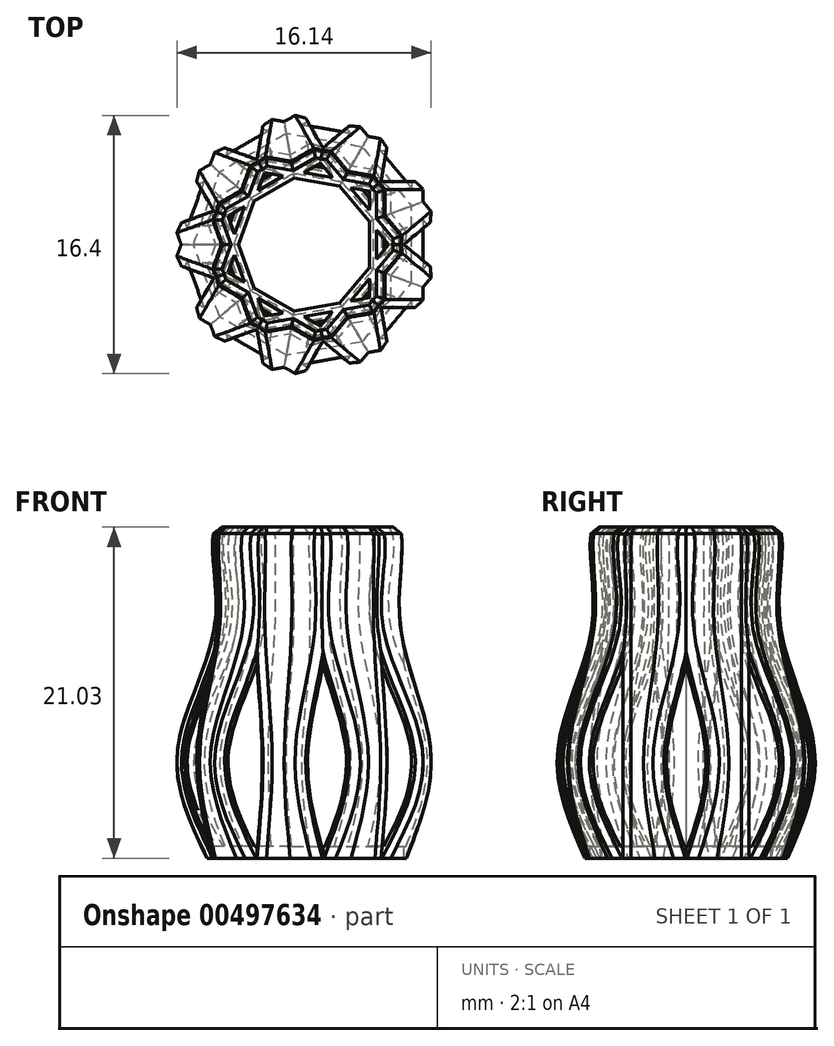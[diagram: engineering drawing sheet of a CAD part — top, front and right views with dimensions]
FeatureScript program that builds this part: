
annotation { "Feature Type Name" : "Feature", "Feature Type Description" : "" }
export const myFeature = defineFeature(function(context is Context, id is Id, definition is map)
    precondition{}
    {
        {
            var Q0;
            Q0=qCreatedBy(makeId("Front.planeOp"),FACE);
            var sketch = newSketch(context, id + "F0", { "sketchPlane" : qUnion([Q0])});
            skLineSegment(sketch, "E0", {"start": v(0, 0) * mm, "end": v(5.4, 0) * mm});
            skLineSegment(sketch, "E1", {"start": v(0, 2.1) * mm, "end": v(0, 0) * mm});
            skLineSegment(sketch, "E2.0", {"start": v(0, 0.75) * mm, "end": v(4.94, 0.75) * mm});
            skFitSpline(sketch, "E3", {"points": [v(5.4, 0) * mm, v(7.42, 6.77) * mm, v(4.86, 15) * mm, v(4.86, 21.03) * mm, v(2.2, 23.07) * mm], "startDerivative": vector(12.6, 24.53) * mm, "endDerivative": vector(-18.36, 8.19) * mm});
            skFitSpline(sketch, "E4.0", {"points": [v(4.73, 0.34) * mm, v(5, 0.85) * mm, v(5.52, 1.86) * mm, v(6.17, 3.35) * mm, v(6.54, 4.57) * mm, v(6.69, 5.53) * mm, v(6.72, 6.25) * mm, v(6.65, 6.97) * mm, v(6.5, 7.74) * mm, v(6.25, 8.54) * mm, v(5.85, 9.64) * mm, v(5.37, 10.8) * mm, v(4.9, 11.99) * mm, v(4.57, 12.9) * mm, v(4.3, 13.83) * mm, v(4.14, 14.63) * mm, v(4.07, 15.28) * mm, v(4.04, 15.91) * mm, v(4.05, 17) * mm, v(4.17, 18.14) * mm, v(4.26, 19.14) * mm, v(4.3, 19.8) * mm, v(4.27, 20.26) * mm, v(4.22, 20.56) * mm, v(4.17, 20.75) * mm, v(4.1, 20.9) * mm, v(3.98, 21.1) * mm, v(3.77, 21.34) * mm, v(3.42, 21.62) * mm, v(2.83, 21.97) * mm, v(2.28, 22.22) * mm, v(1.9, 22.39) * mm]});
            skLineSegment(sketch, "E5", {"start": v(1.9, 22.39) * mm, "end": v(3.6, 22.39) * mm});
            skPoint(sketch, "E6.orphan", {"position": v(4.86, 0.75) * mm});
            skLineSegment(sketch, "E7", {"start": v(4.86, 21.03) * mm, "end": v(2.46, 21.03) * mm});
            skSolve(sketch);
        }
        {
            var Q0;
            {var subQ2=sQuery(id+"F0.wireOp",EDGE,"E0");Q0=makeQuery(id+"F0.imprint","IMPRINT",FACE,{"disambiguationData":[TD([[makeQuery(id+"F0.imprint","IMPRINT",EDGE,{"derivedFrom":subQ2}),1.0]])]});}
            extrude(context, id + "F1", {"entities" : qUnion([Q0]), "depth" : 4 * mm, "hasSecondDirection" : true, "secondDirectionOppositeDirection" : true, "secondDirectionDepth" : 4 * mm});
        }
        {
            var Q0;
            Q0=makeQuery(id+"F1.opExtrude","CAP_EDGE",EDGE,{"disambiguationData":[OSD([sQuery(id+"F0.wireOp",EDGE,"E3")])],"isStart":false});
            var Q1;
            Q1=makeQuery(id+"F1.opExtrude","CAP_EDGE",EDGE,{"disambiguationData":[OSD([sQuery(id+"F0.wireOp",EDGE,"E3")])],"isStart":true});
            chamfer(context, id + "F2", {"entities" : qUnion([Q0, Q1]), "width" : 0.5 * mm});
        }
        {
            var Q0;
            {var subQ0=sQuery(id+"F0.wireOp",EDGE,"E7");var subQ3=makeQuery(id+"F1.opExtrude","SWEPT_FACE",FACE,{"disambiguationData":[OSD([sQuery(id+"F0.wireOp",EDGE,"E4.0")])]});var subQ4=sQuery(id+"F0.wireOp",EDGE,"E3");Q0=makeQuery(id+"F5.opBoolean","SPLIT",EDGE,{"disambiguationData":[TD([makeQuery(id+"F4.opPattern","COPY",FACE,{"derivedFrom":subQ3,"instanceName":"1"})])],"derivedFrom":makeQuery(id+"F1.opExtrude","SWEPT_EDGE",EDGE,{"disambiguationData":[OSD([subQ4,subQ0])]})});}
            var Q1;
            {var subQ0=sQuery(id+"F0.wireOp",EDGE,"E7");var subQ3=sQuery(id+"F0.wireOp",EDGE,"E3");var subQ4=makeQuery(id+"F1.opExtrude","SWEPT_FACE",FACE,{"disambiguationData":[OSD([subQ3])]});Q1=makeQuery(id+"F5.opBoolean","SPLIT",EDGE,{"disambiguationData":[TD([makeQuery(id+"F4.opPattern","COPY",FACE,{"derivedFrom":subQ4,"instanceName":"1"})])],"derivedFrom":makeQuery(id+"F1.opExtrude","SWEPT_EDGE",EDGE,{"disambiguationData":[OSD([subQ3,subQ0])]})});}
            var Q2;
            {var subQ0=sQuery(id+"F0.wireOp",EDGE,"E7");var subQ3=sQuery(id+"F0.wireOp",EDGE,"E3");var subQ4=makeQuery(id+"F1.opExtrude","SWEPT_FACE",FACE,{"disambiguationData":[OSD([subQ3])]});Q2=makeQuery(id+"F5.opBoolean","SPLIT",EDGE,{"disambiguationData":[TD([makeQuery(id+"F4.opPattern","COPY",FACE,{"derivedFrom":subQ4,"instanceName":"8"})])],"derivedFrom":makeQuery(id+"F1.opExtrude","SWEPT_EDGE",EDGE,{"disambiguationData":[OSD([subQ3,subQ0])]})});}
            var Q3;
            Q3=makeQuery(id+"F1.opExtrude","CAP_EDGE",EDGE,{"disambiguationData":[OSD([sQuery(id+"F0.wireOp",EDGE,"E7")])],"isStart":true});
            var Q4;
            Q4=makeQuery(id+"F2.opChamfer","BLEND_EDGE",EDGE,{"blendedFrom":[makeQuery(id+"F1.opExtrude","CAP_EDGE",EDGE,{"disambiguationData":[OSD([sQuery(id+"F0.wireOp",EDGE,"E3")])],"isStart":true}),makeQuery(id+"F1.opExtrude","SWEPT_FACE",FACE,{"disambiguationData":[OSD([sQuery(id+"F0.wireOp",EDGE,"E7")])]})],"blendedInto":[makeQuery(id+"F1.opExtrude","SWEPT_FACE",FACE,{"disambiguationData":[OSD([sQuery(id+"F0.wireOp",EDGE,"E7")])]})]});
            var Q5;
            Q5=makeQuery(id+"F2.opChamfer","BLEND_EDGE",EDGE,{"blendedFrom":[makeQuery(id+"F1.opExtrude","CAP_EDGE",EDGE,{"disambiguationData":[OSD([sQuery(id+"F0.wireOp",EDGE,"E3")])],"isStart":false}),makeQuery(id+"F1.opExtrude","SWEPT_FACE",FACE,{"disambiguationData":[OSD([sQuery(id+"F0.wireOp",EDGE,"E7")])]})],"blendedInto":[makeQuery(id+"F1.opExtrude","SWEPT_FACE",FACE,{"disambiguationData":[OSD([sQuery(id+"F0.wireOp",EDGE,"E7")])]})]});
            var Q6;
            Q6=makeQuery(id+"F1.opExtrude","CAP_EDGE",EDGE,{"disambiguationData":[OSD([sQuery(id+"F0.wireOp",EDGE,"E7")])],"isStart":false});
            chamfer(context, id + "F3", {"entities" : qUnion([Q0, Q1, Q2, Q3, Q4, Q5, Q6]), "width" : 0.5 * mm, "tangentPropagation" : true});
        }
        {
            var Q0;
            Q0=makeQuery(id+"F1.opExtrude","SWEPT_BODY",BODY,{"disambiguationData":[OSD([sQuery(id+"F0.wireOp",EDGE,"E0"),sQuery(id+"F0.wireOp",EDGE,"T7crRCSO-nWGS-oMrG-bt7b-a5VfY8CambFn"),sQuery(id+"F0.wireOp",EDGE,"xv8VgBhu-qazy-YgqB-v8JE-5yVdrMK1Qche"),sQuery(id+"F0.wireOp",EDGE,"17f4b7c3-1163-45f6-bf05-4113330963bc.0"),sQuery(id+"F0.wireOp",EDGE,"17f4b7c3-1163-45f6-bf05-4113330963bc.1"),sQuery(id+"F0.wireOp",EDGE,"17f4b7c3-1163-45f6-bf05-4113330963bc.2"),sQuery(id+"F0.wireOp",EDGE,"8E1QmZ2g-YMvP-tSYN-84yT-wLBnS1EG7rmy"),sQuery(id+"F0.wireOp",EDGE,"E1")])]});
            var Q1;
            Q1=sQuery(id+"F0.wireOp",EDGE,"E1");
            circularPattern(context, id + "F4", {"entities" : qUnion([Q0]), "axis" : qUnion([Q1]), "angle" : 360 * degree, "instanceCount" : 9, "equalSpace" : true});
        }
        {
            var Q0;
            Q0=makeQuery(id+"F4.opPattern","COPY",BODY,{"derivedFrom":makeQuery(id+"F1.opExtrude","SWEPT_BODY",BODY,{"disambiguationData":[OSD([sQuery(id+"F0.wireOp",EDGE,"E0"),sQuery(id+"F0.wireOp",EDGE,"T7crRCSO-nWGS-oMrG-bt7b-a5VfY8CambFn"),sQuery(id+"F0.wireOp",EDGE,"17f4b7c3-1163-45f6-bf05-4113330963bc.1"),sQuery(id+"F0.wireOp",EDGE,"17f4b7c3-1163-45f6-bf05-4113330963bc.2"),sQuery(id+"F0.wireOp",EDGE,"E1"),sQuery(id+"F0.wireOp",EDGE,"RQvKXf4q-lE5c-LyfI-oZmB-OhUsM85Rd2iv")])]}),"instanceName":"1"});
            var Q1;
            Q1=makeQuery(id+"F4.opPattern","COPY",BODY,{"derivedFrom":makeQuery(id+"F1.opExtrude","SWEPT_BODY",BODY,{"disambiguationData":[OSD([sQuery(id+"F0.wireOp",EDGE,"E0"),sQuery(id+"F0.wireOp",EDGE,"T7crRCSO-nWGS-oMrG-bt7b-a5VfY8CambFn"),sQuery(id+"F0.wireOp",EDGE,"17f4b7c3-1163-45f6-bf05-4113330963bc.1"),sQuery(id+"F0.wireOp",EDGE,"17f4b7c3-1163-45f6-bf05-4113330963bc.2"),sQuery(id+"F0.wireOp",EDGE,"E1"),sQuery(id+"F0.wireOp",EDGE,"RQvKXf4q-lE5c-LyfI-oZmB-OhUsM85Rd2iv")])]}),"instanceName":"12"});
            var Q2;
            Q2=makeQuery(id+"F4.opPattern","COPY",BODY,{"derivedFrom":makeQuery(id+"F1.opExtrude","SWEPT_BODY",BODY,{"disambiguationData":[OSD([sQuery(id+"F0.wireOp",EDGE,"E0"),sQuery(id+"F0.wireOp",EDGE,"T7crRCSO-nWGS-oMrG-bt7b-a5VfY8CambFn"),sQuery(id+"F0.wireOp",EDGE,"17f4b7c3-1163-45f6-bf05-4113330963bc.1"),sQuery(id+"F0.wireOp",EDGE,"17f4b7c3-1163-45f6-bf05-4113330963bc.2"),sQuery(id+"F0.wireOp",EDGE,"E1"),sQuery(id+"F0.wireOp",EDGE,"RQvKXf4q-lE5c-LyfI-oZmB-OhUsM85Rd2iv")])]}),"instanceName":"13"});
            var Q3;
            Q3=makeQuery(id+"F4.opPattern","COPY",BODY,{"derivedFrom":makeQuery(id+"F1.opExtrude","SWEPT_BODY",BODY,{"disambiguationData":[OSD([sQuery(id+"F0.wireOp",EDGE,"E0"),sQuery(id+"F0.wireOp",EDGE,"T7crRCSO-nWGS-oMrG-bt7b-a5VfY8CambFn"),sQuery(id+"F0.wireOp",EDGE,"17f4b7c3-1163-45f6-bf05-4113330963bc.1"),sQuery(id+"F0.wireOp",EDGE,"17f4b7c3-1163-45f6-bf05-4113330963bc.2"),sQuery(id+"F0.wireOp",EDGE,"E1"),sQuery(id+"F0.wireOp",EDGE,"RQvKXf4q-lE5c-LyfI-oZmB-OhUsM85Rd2iv")])]}),"instanceName":"11"});
            var Q4;
            Q4=makeQuery(id+"F4.opPattern","COPY",BODY,{"derivedFrom":makeQuery(id+"F1.opExtrude","SWEPT_BODY",BODY,{"disambiguationData":[OSD([sQuery(id+"F0.wireOp",EDGE,"E0"),sQuery(id+"F0.wireOp",EDGE,"T7crRCSO-nWGS-oMrG-bt7b-a5VfY8CambFn"),sQuery(id+"F0.wireOp",EDGE,"17f4b7c3-1163-45f6-bf05-4113330963bc.1"),sQuery(id+"F0.wireOp",EDGE,"17f4b7c3-1163-45f6-bf05-4113330963bc.2"),sQuery(id+"F0.wireOp",EDGE,"E1"),sQuery(id+"F0.wireOp",EDGE,"RQvKXf4q-lE5c-LyfI-oZmB-OhUsM85Rd2iv")])]}),"instanceName":"3"});
            var Q5;
            Q5=makeQuery(id+"F4.opPattern","COPY",BODY,{"derivedFrom":makeQuery(id+"F1.opExtrude","SWEPT_BODY",BODY,{"disambiguationData":[OSD([sQuery(id+"F0.wireOp",EDGE,"E0"),sQuery(id+"F0.wireOp",EDGE,"T7crRCSO-nWGS-oMrG-bt7b-a5VfY8CambFn"),sQuery(id+"F0.wireOp",EDGE,"17f4b7c3-1163-45f6-bf05-4113330963bc.1"),sQuery(id+"F0.wireOp",EDGE,"17f4b7c3-1163-45f6-bf05-4113330963bc.2"),sQuery(id+"F0.wireOp",EDGE,"E1"),sQuery(id+"F0.wireOp",EDGE,"RQvKXf4q-lE5c-LyfI-oZmB-OhUsM85Rd2iv")])]}),"instanceName":"2"});
            var Q6;
            Q6=makeQuery(id+"F4.opPattern","COPY",BODY,{"derivedFrom":makeQuery(id+"F1.opExtrude","SWEPT_BODY",BODY,{"disambiguationData":[OSD([sQuery(id+"F0.wireOp",EDGE,"E0"),sQuery(id+"F0.wireOp",EDGE,"T7crRCSO-nWGS-oMrG-bt7b-a5VfY8CambFn"),sQuery(id+"F0.wireOp",EDGE,"17f4b7c3-1163-45f6-bf05-4113330963bc.1"),sQuery(id+"F0.wireOp",EDGE,"17f4b7c3-1163-45f6-bf05-4113330963bc.2"),sQuery(id+"F0.wireOp",EDGE,"E1"),sQuery(id+"F0.wireOp",EDGE,"RQvKXf4q-lE5c-LyfI-oZmB-OhUsM85Rd2iv")])]}),"instanceName":"4"});
            var Q7;
            Q7=makeQuery(id+"F4.opPattern","COPY",BODY,{"derivedFrom":makeQuery(id+"F1.opExtrude","SWEPT_BODY",BODY,{"disambiguationData":[OSD([sQuery(id+"F0.wireOp",EDGE,"E0"),sQuery(id+"F0.wireOp",EDGE,"T7crRCSO-nWGS-oMrG-bt7b-a5VfY8CambFn"),sQuery(id+"F0.wireOp",EDGE,"17f4b7c3-1163-45f6-bf05-4113330963bc.1"),sQuery(id+"F0.wireOp",EDGE,"17f4b7c3-1163-45f6-bf05-4113330963bc.2"),sQuery(id+"F0.wireOp",EDGE,"E1"),sQuery(id+"F0.wireOp",EDGE,"RQvKXf4q-lE5c-LyfI-oZmB-OhUsM85Rd2iv")])]}),"instanceName":"7"});
            var Q8;
            Q8=makeQuery(id+"F1.opExtrude","SWEPT_BODY",BODY,{"disambiguationData":[OSD([sQuery(id+"F0.wireOp",EDGE,"E0"),sQuery(id+"F0.wireOp",EDGE,"T7crRCSO-nWGS-oMrG-bt7b-a5VfY8CambFn"),sQuery(id+"F0.wireOp",EDGE,"17f4b7c3-1163-45f6-bf05-4113330963bc.1"),sQuery(id+"F0.wireOp",EDGE,"17f4b7c3-1163-45f6-bf05-4113330963bc.2"),sQuery(id+"F0.wireOp",EDGE,"E1"),sQuery(id+"F0.wireOp",EDGE,"RQvKXf4q-lE5c-LyfI-oZmB-OhUsM85Rd2iv")])]});
            var Q9;
            Q9=makeQuery(id+"F4.opPattern","COPY",BODY,{"derivedFrom":makeQuery(id+"F1.opExtrude","SWEPT_BODY",BODY,{"disambiguationData":[OSD([sQuery(id+"F0.wireOp",EDGE,"E0"),sQuery(id+"F0.wireOp",EDGE,"T7crRCSO-nWGS-oMrG-bt7b-a5VfY8CambFn"),sQuery(id+"F0.wireOp",EDGE,"17f4b7c3-1163-45f6-bf05-4113330963bc.1"),sQuery(id+"F0.wireOp",EDGE,"17f4b7c3-1163-45f6-bf05-4113330963bc.2"),sQuery(id+"F0.wireOp",EDGE,"E1"),sQuery(id+"F0.wireOp",EDGE,"RQvKXf4q-lE5c-LyfI-oZmB-OhUsM85Rd2iv")])]}),"instanceName":"10"});
            var Q10;
            Q10=makeQuery(id+"F4.opPattern","COPY",BODY,{"derivedFrom":makeQuery(id+"F1.opExtrude","SWEPT_BODY",BODY,{"disambiguationData":[OSD([sQuery(id+"F0.wireOp",EDGE,"E0"),sQuery(id+"F0.wireOp",EDGE,"T7crRCSO-nWGS-oMrG-bt7b-a5VfY8CambFn"),sQuery(id+"F0.wireOp",EDGE,"17f4b7c3-1163-45f6-bf05-4113330963bc.1"),sQuery(id+"F0.wireOp",EDGE,"17f4b7c3-1163-45f6-bf05-4113330963bc.2"),sQuery(id+"F0.wireOp",EDGE,"E1"),sQuery(id+"F0.wireOp",EDGE,"RQvKXf4q-lE5c-LyfI-oZmB-OhUsM85Rd2iv")])]}),"instanceName":"5"});
            var Q11;
            Q11=makeQuery(id+"F4.opPattern","COPY",BODY,{"derivedFrom":makeQuery(id+"F1.opExtrude","SWEPT_BODY",BODY,{"disambiguationData":[OSD([sQuery(id+"F0.wireOp",EDGE,"E0"),sQuery(id+"F0.wireOp",EDGE,"T7crRCSO-nWGS-oMrG-bt7b-a5VfY8CambFn"),sQuery(id+"F0.wireOp",EDGE,"17f4b7c3-1163-45f6-bf05-4113330963bc.1"),sQuery(id+"F0.wireOp",EDGE,"17f4b7c3-1163-45f6-bf05-4113330963bc.2"),sQuery(id+"F0.wireOp",EDGE,"E1"),sQuery(id+"F0.wireOp",EDGE,"RQvKXf4q-lE5c-LyfI-oZmB-OhUsM85Rd2iv")])]}),"instanceName":"9"});
            var Q12;
            Q12=makeQuery(id+"F4.opPattern","COPY",BODY,{"derivedFrom":makeQuery(id+"F1.opExtrude","SWEPT_BODY",BODY,{"disambiguationData":[OSD([sQuery(id+"F0.wireOp",EDGE,"E0"),sQuery(id+"F0.wireOp",EDGE,"T7crRCSO-nWGS-oMrG-bt7b-a5VfY8CambFn"),sQuery(id+"F0.wireOp",EDGE,"17f4b7c3-1163-45f6-bf05-4113330963bc.1"),sQuery(id+"F0.wireOp",EDGE,"17f4b7c3-1163-45f6-bf05-4113330963bc.2"),sQuery(id+"F0.wireOp",EDGE,"E1"),sQuery(id+"F0.wireOp",EDGE,"RQvKXf4q-lE5c-LyfI-oZmB-OhUsM85Rd2iv")])]}),"instanceName":"8"});
            var Q13;
            Q13=makeQuery(id+"F4.opPattern","COPY",BODY,{"derivedFrom":makeQuery(id+"F1.opExtrude","SWEPT_BODY",BODY,{"disambiguationData":[OSD([sQuery(id+"F0.wireOp",EDGE,"E0"),sQuery(id+"F0.wireOp",EDGE,"T7crRCSO-nWGS-oMrG-bt7b-a5VfY8CambFn"),sQuery(id+"F0.wireOp",EDGE,"17f4b7c3-1163-45f6-bf05-4113330963bc.1"),sQuery(id+"F0.wireOp",EDGE,"17f4b7c3-1163-45f6-bf05-4113330963bc.2"),sQuery(id+"F0.wireOp",EDGE,"E1"),sQuery(id+"F0.wireOp",EDGE,"RQvKXf4q-lE5c-LyfI-oZmB-OhUsM85Rd2iv")])]}),"instanceName":"6"});
            booleanBodies(context, id + "F5", {"operationType" : BooleanOperationType.UNION, "tools" : qUnion([Q0, Q1, Q2, Q3, Q4, Q5, Q6, Q7, Q8, Q9, Q10, Q11, Q12, Q13])});
        }
    });
